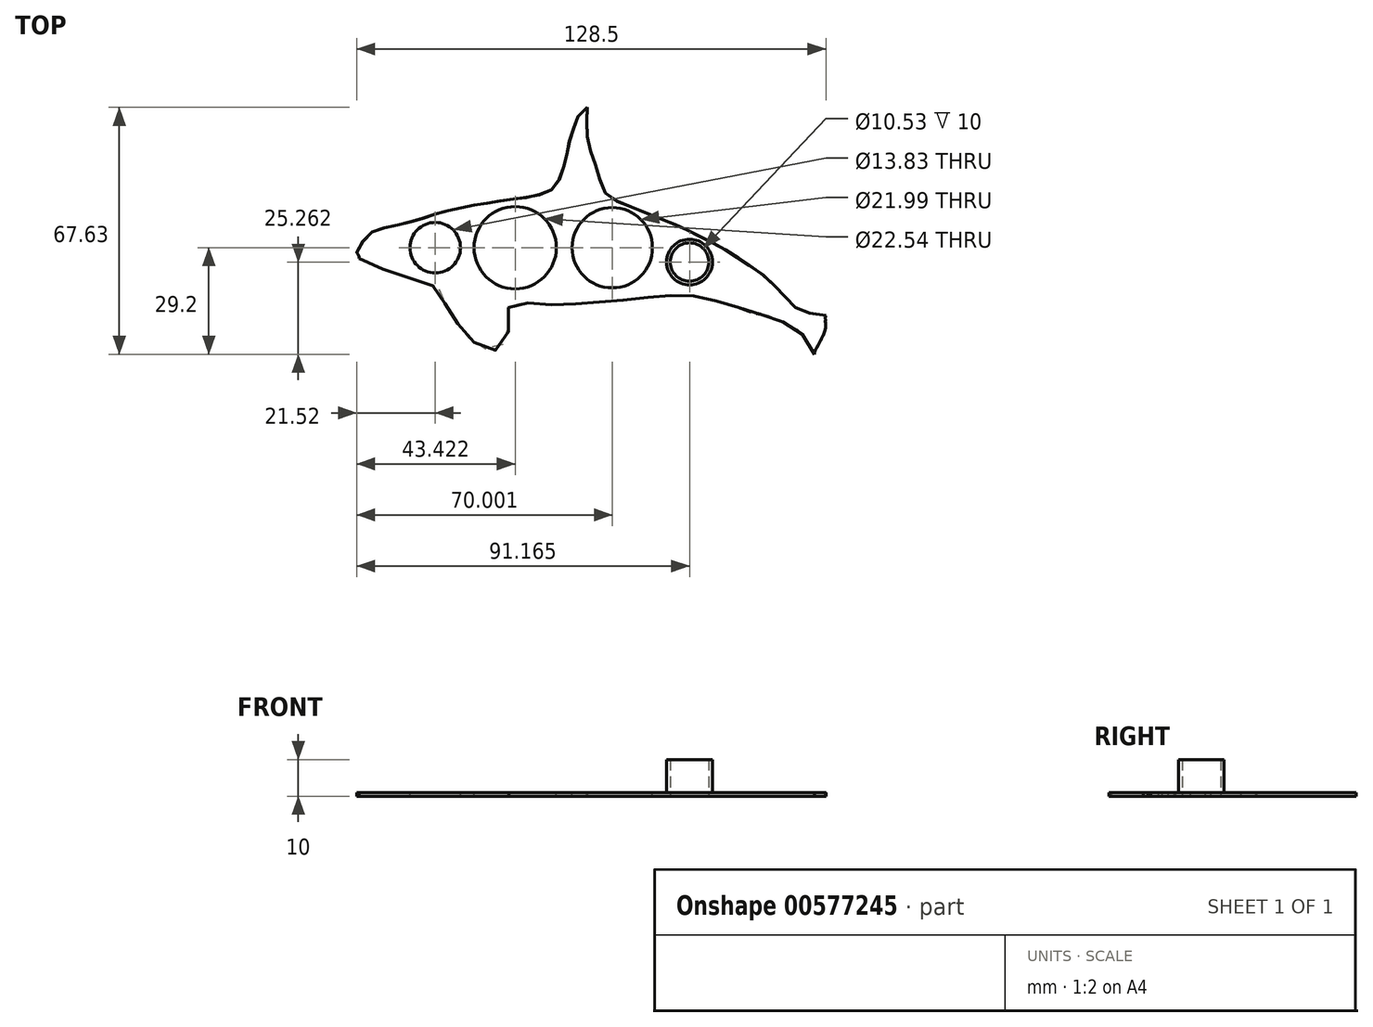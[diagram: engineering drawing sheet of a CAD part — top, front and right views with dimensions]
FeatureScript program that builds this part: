
annotation { "Feature Type Name" : "Feature", "Feature Type Description" : "" }
export const myFeature = defineFeature(function(context is Context, id is Id, definition is map)
    precondition{}
    {
        {
            var Q0;
            Q0=qCreatedBy(makeId("Top.planeOp"),FACE);
            var sketch = newSketch(context, id + "F0", { "sketchPlane" : qUnion([Q0])});
            skFitSpline(sketch, "E0", {"points": [v(-64.38, -1.3) * mm, v(-64, -0.76) * mm, v(-63.32, 0) * mm, v(-62.94, 1.27) * mm, v(-61.5, 3.09) * mm, v(-59.4, 5.12) * mm, v(-56.22, 6.33) * mm, v(-52.45, 7.16) * mm, v(-45.96, 8.82) * mm, v(-40.82, 10.48) * mm, v(-36.6, 11.46) * mm, v(-32.3, 12.45) * mm, v(-27.46, 13.2) * mm, v(-22.93, 13.96) * mm, v(-19, 14.4) * mm, v(-15.84, 14.94) * mm, v(-11.84, 15.92) * mm, v(-9.5, 17.35) * mm, v(-8.06, 20.3) * mm, v(-7.08, 23.32) * mm, v(-5.65, 30) * mm, v(-4.39, 33.64) * mm, v(-2.88, 37.3) * mm, v(0, 39.43) * mm, v(1.02, 38.67) * mm, v(1.02, 35.78) * mm, v(0.9, 33.27) * mm, v(0.9, 31.25) * mm, v(1.15, 30) * mm, v(1.9, 26.72) * mm, v(3.41, 22.45) * mm, v(5.05, 17.04) * mm, v(5.68, 15.78) * mm, v(6.8, 14.65) * mm, v(12.25, 12.14) * mm, v(26.68, 6.26) * mm, v(31.47, 3.9) * mm, v(37.41, 0.83) * mm, v(44.7, -3.83) * mm, v(49.49, -7.15) * mm, v(51.28, -8.88) * mm, v(54.43, -12.2) * mm, v(56.43, -14.2) * mm, v(57.07, -14.9) * mm, v(57.61, -15.55) * mm, v(58.26, -16.03) * mm, v(59.8, -16.86) * mm, v(62.16, -16.81) * mm, v(64.02, -16.96) * mm, v(64.92, -17.11) * mm, v(65.78, -17.61) * mm, v(66.48, -18.47) * mm, v(66.28, -19.07) * mm, v(66.27, -19.58) * mm, v(66.29, -20.05) * mm, v(66.27, -20.05) * mm, v(66.28, -20.93) * mm, v(66.28, -22.08) * mm, v(65.73, -24.04) * mm, v(64.57, -26.35) * mm, v(63.87, -27.66) * mm, v(63.4, -28.43) * mm, v(63.31, -29.1) * mm, v(63.31, -29.53) * mm, v(63.26, -29.53) * mm, v(62.92, -30.49) * mm, v(62.03, -30.2) * mm, v(61.27, -29.72) * mm, v(60.5, -28.84) * mm, v(60.02, -27.47) * mm, v(58.21, -24.41) * mm, v(56.65, -23.04) * mm, v(55.2, -22.3) * mm, v(53.56, -21.34) * mm, v(51.55, -20.5) * mm, v(48.8, -19.48) * mm, v(45.58, -18.9) * mm, v(41.71, -17.53) * mm, v(35.88, -15.72) * mm, v(33.9, -15.28) * mm, v(29.74, -14.28) * mm, v(22.11, -14.14) * mm, v(14, -14.96) * mm, v(6.05, -15.73) * mm, v(-3.99, -16.45) * mm, v(-11.47, -16.6) * mm, v(-19.75, -15.69) * mm, v(-20.41, -15.69) * mm, v(-20.5, -16.27) * mm, v(-20.44, -19.53) * mm, v(-20.52, -23.13) * mm, v(-20.58, -24.84) * mm, v(-21.1, -25.84) * mm, v(-24.48, -28.89) * mm, v(-25.58, -29.4) * mm, v(-27.38, -28.97) * mm, v(-29.65, -28.1) * mm, v(-31.92, -26.42) * mm, v(-34.47, -23.64) * mm, v(-37.44, -19.8) * mm, v(-39.67, -16.09) * mm, v(-40.38, -14.48) * mm, v(-40.53, -12.05) * mm, v(-40.7, -11.94) * mm, v(-41.4, -11.74) * mm, v(-50.94, -8.58) * mm, v(-56.5, -6.73) * mm, v(-62.05, -4.65) * mm, v(-63.45, -3.17) * mm, v(-63.53, -2.43) * mm, v(-64.38, -1.3) * mm]});
            skCircle(sketch, "E1", {"center": v(-41.59, 0) * mm, "radius": 5.92 * mm});
            skCircle(sketch, "E2", {"center": v(-19.69, 0) * mm, "radius": 10.27 * mm});
            skCircle(sketch, "E3", {"center": v(6.9, 0) * mm, "radius": 10 * mm});
            skCircle(sketch, "E4", {"center": v(28.05, -3.94) * mm, "radius": 5.27 * mm});
            skSolve(sketch);
        }
        {
            var Q0;
            Q0=makeQuery(id+"F0.imprint","IMPRINT",FACE,{"disambiguationData":[TD([[makeQuery(id+"F0.imprint","IMPRINT",EDGE,{"derivedFrom":sQuery(id+"F0.wireOp",EDGE,"E0")}),-1.0]])]});
            extrude(context, id + "F1", {"entities" : qUnion([Q0]), "depth" : 10 * mm, "offsetDistance" : 25 * mm});
        }
        {
            var Q0;
            Q0=makeQuery(id+"F1.opExtrude","CAP_FACE",FACE,{"disambiguationData":[OSD([sQuery(id+"F0.wireOp",EDGE,"E0")])],"isStart":false});
            shell(context, id + "F2", {"entities" : qUnion([Q0]), "thickness" : 1 * mm});
        }
        {
            var Q0;
            {var subQ0=sQuery(id+"F0.wireOp",EDGE,"E4");var subQ1=sQuery(id+"F0.wireOp",EDGE,"E3");var subQ2=sQuery(id+"F0.wireOp",EDGE,"E2");var subQ3=sQuery(id+"F0.wireOp",EDGE,"E1");var subQ4=sQuery(id+"F0.wireOp",EDGE,"E0");Q0=makeQuery(id+"F2.opShell","OFFSET_FACE",FACE,{"disambiguationData":[OSD([subQ4,subQ3,subQ2,subQ1,subQ0]),TDD([makeQuery(id+"F1.opExtrude","CAP_FACE",FACE,{"disambiguationData":[OSD([subQ4,subQ3,subQ2,subQ1,subQ0])],"isStart":false})]),OD(0.0)]});}
            var Q1;
            {var subQ0=sQuery(id+"F0.wireOp",EDGE,"E4");var subQ1=sQuery(id+"F0.wireOp",EDGE,"E3");var subQ2=sQuery(id+"F0.wireOp",EDGE,"E2");var subQ3=sQuery(id+"F0.wireOp",EDGE,"E1");var subQ4=sQuery(id+"F0.wireOp",EDGE,"E0");Q1=makeQuery(id+"F2.opShell","OFFSET_FACE",FACE,{"disambiguationData":[OSD([subQ4,subQ3,subQ2,subQ1,subQ0]),TDD([makeQuery(id+"F1.opExtrude","CAP_FACE",FACE,{"disambiguationData":[OSD([subQ4,subQ3,subQ2,subQ1,subQ0])],"isStart":false})]),OD(1.0)]});}
            var Q2;
            {var subQ0=sQuery(id+"F0.wireOp",EDGE,"E4");var subQ1=sQuery(id+"F0.wireOp",EDGE,"E3");var subQ2=sQuery(id+"F0.wireOp",EDGE,"E2");var subQ3=sQuery(id+"F0.wireOp",EDGE,"E1");var subQ4=sQuery(id+"F0.wireOp",EDGE,"E0");Q2=makeQuery(id+"F2.opShell","OFFSET_FACE",FACE,{"disambiguationData":[OSD([subQ4,subQ3,subQ2,subQ1,subQ0]),TDD([makeQuery(id+"F1.opExtrude","CAP_FACE",FACE,{"disambiguationData":[OSD([subQ4,subQ3,subQ2,subQ1,subQ0])],"isStart":false})]),OD(2.0)]});}
            var Q3;
            {var subQ0=sQuery(id+"F0.wireOp",EDGE,"E4");var subQ1=sQuery(id+"F0.wireOp",EDGE,"E3");var subQ2=sQuery(id+"F0.wireOp",EDGE,"E2");var subQ3=sQuery(id+"F0.wireOp",EDGE,"E1");var subQ4=sQuery(id+"F0.wireOp",EDGE,"E0");Q3=makeQuery(id+"F2.opShell","OFFSET_FACE",FACE,{"disambiguationData":[OSD([subQ4,subQ3,subQ2,subQ1,subQ0]),TDD([makeQuery(id+"F1.opExtrude","CAP_FACE",FACE,{"disambiguationData":[OSD([subQ4,subQ3,subQ2,subQ1,subQ0])],"isStart":false})]),OD(3.0)]});}
            extrude(context, id + "F3", {"entities" : qUnion([Q0, Q1, Q2, Q3]), "operationType" : NewBodyOperationType.REMOVE, "oppositeDirection" : true, "depth" : 25 * mm, "offsetDistance" : 25 * mm});
        }
    });
